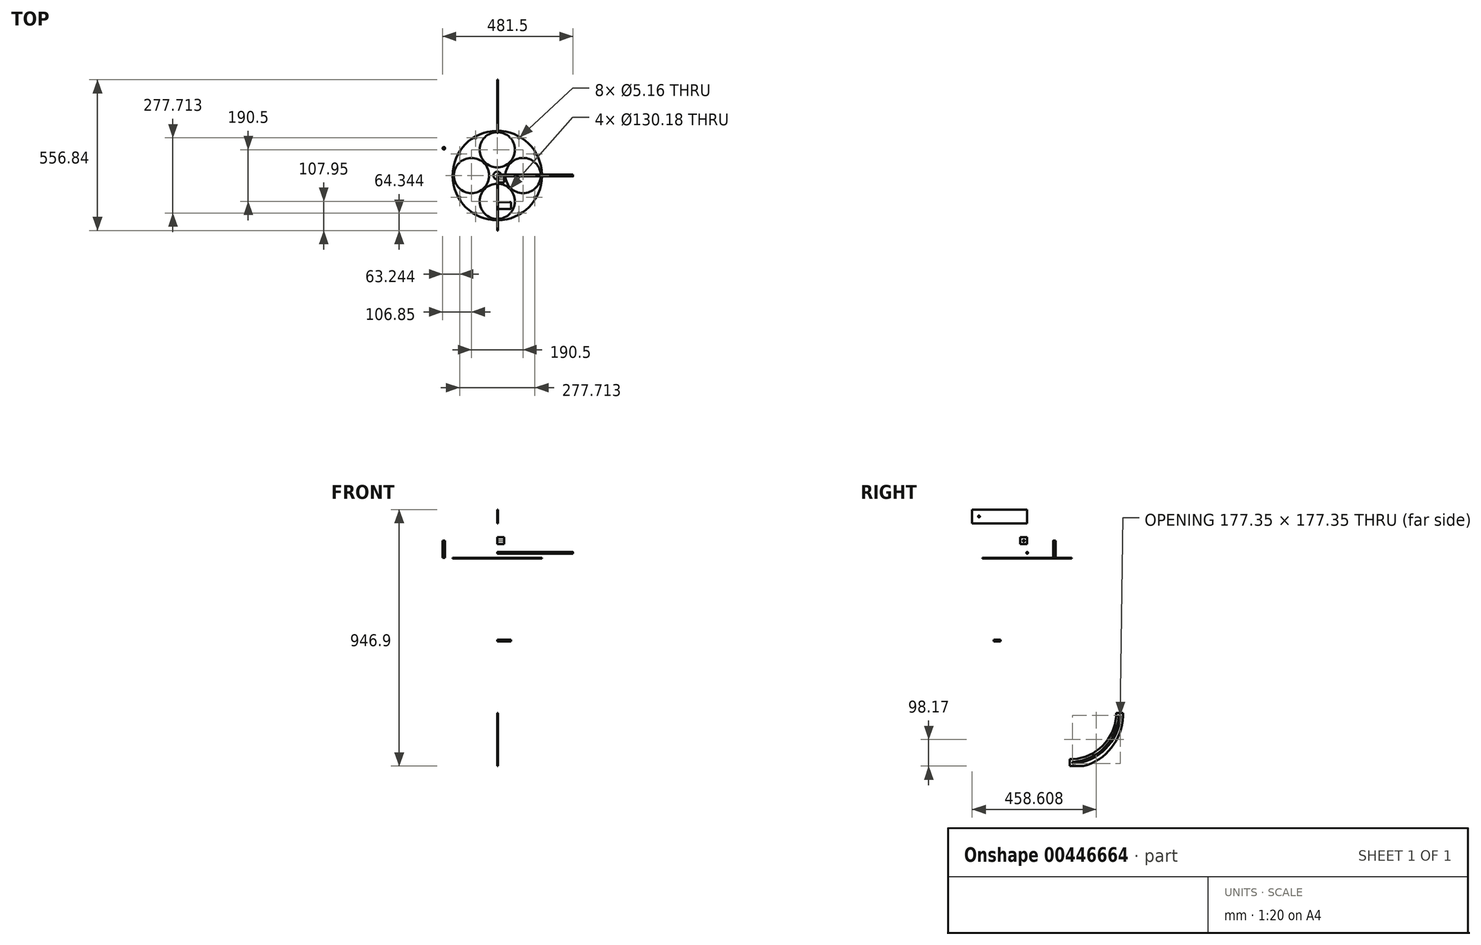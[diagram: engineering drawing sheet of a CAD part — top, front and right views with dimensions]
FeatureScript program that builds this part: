
annotation { "Feature Type Name" : "Feature", "Feature Type Description" : "" }
export const myFeature = defineFeature(function(context is Context, id is Id, definition is map)
    precondition{}
    {
        {
            var Q0;
            Q0=qCreatedBy(makeId("Top.planeOp"),FACE);
            var sketch = newSketch(context, id + "F0", { "sketchPlane" : qUnion([Q0])});
            skCircle(sketch, "E0", {"center": v(0, 0) * mm, "radius": 165.1 * mm});
            skCircle(sketch, "E1", {"center": v(0, 95.25) * mm, "radius": 65.09 * mm});
            skCircle(sketch, "E2", {"center": v(95.25, 0) * mm, "radius": 65.09 * mm});
            skCircle(sketch, "E3", {"center": v(0, -95.25) * mm, "radius": 65.09 * mm});
            skCircle(sketch, "E4", {"center": v(-95.25, 0) * mm, "radius": 65.09 * mm});
            skCircle(sketch, "E5", {"center": v(138.86, 80.17) * mm, "radius": 2.58 * mm});
            skCircle(sketch, "E6.1.0", {"center": v(80.17, 138.86) * mm, "radius": 2.58 * mm});
            skCircle(sketch, "E7.1.3.0", {"center": v(-80.17, 138.86) * mm, "radius": 2.58 * mm});
            skCircle(sketch, "E7.1.4.0", {"center": v(-138.86, 80.17) * mm, "radius": 2.58 * mm});
            skCircle(sketch, "E7.1.6.0", {"center": v(-138.86, -80.17) * mm, "radius": 2.58 * mm});
            skCircle(sketch, "E7.1.7.0", {"center": v(-80.17, -138.86) * mm, "radius": 2.58 * mm});
            skCircle(sketch, "E8.1.9.0", {"center": v(80.17, -138.86) * mm, "radius": 2.58 * mm});
            skCircle(sketch, "E8.1.10.0", {"center": v(138.86, -80.17) * mm, "radius": 2.58 * mm});
            skCircle(sketch, "E9", {"center": v(0, 0) * mm, "radius": 14.22 * mm});
            skSolve(sketch);
        }
        {
            var Q0;
            Q0=makeQuery(id+"F0.imprint","IMPRINT",FACE,{"disambiguationData":[TD([[makeQuery(id+"F0.imprint","IMPRINT",EDGE,{"derivedFrom":sQuery(id+"F0.wireOp",EDGE,"E0")}),1.0]])]});
            extrude(context, id + "F1", {"entities" : qUnion([Q0]), "depth" : 2.54 * mm});
        }
        {
            var Q0;
            Q0=makeQuery(id+"F1.opExtrude","CAP_FACE",FACE,{"disambiguationData":[OSD([sQuery(id+"F0.wireOp",EDGE,"E0"),sQuery(id+"F0.wireOp",EDGE,"E1"),sQuery(id+"F0.wireOp",EDGE,"E2"),sQuery(id+"F0.wireOp",EDGE,"E3"),sQuery(id+"F0.wireOp",EDGE,"E4"),sQuery(id+"F0.wireOp",EDGE,"E5"),sQuery(id+"F0.wireOp",EDGE,"E6.1.0"),sQuery(id+"F0.wireOp",EDGE,"E7.1.3.0"),sQuery(id+"F0.wireOp",EDGE,"E7.1.4.0"),sQuery(id+"F0.wireOp",EDGE,"E7.1.6.0"),sQuery(id+"F0.wireOp",EDGE,"E7.1.7.0"),sQuery(id+"F0.wireOp",EDGE,"E8.1.9.0"),sQuery(id+"F0.wireOp",EDGE,"E8.1.10.0")])],"isStart":false});
            var sketch = newSketch(context, id + "F2", { "sketchPlane" : qUnion([Q0])});
            skCircle(sketch, "E10", {"center": v(-197.34, 100.57) * mm, "radius": 4.76 * mm});
            skSolve(sketch);
        }
        {
            var Q0;
            Q0=makeQuery(id+"F2.imprint","IMPRINT",FACE,{"disambiguationData":[TD([[makeQuery(id+"F2.imprint","IMPRINT",EDGE,{"derivedFrom":sQuery(id+"F2.wireOp",EDGE,"E10")}),1.0]])]});
            extrude(context, id + "F3", {"entities" : qUnion([Q0]), "depth" : 63.5 * mm});
        }
        {
            var Q0;
            Q0=qCreatedBy(makeId("Right.planeOp"),FACE);
            var sketch = newSketch(context, id + "F4", { "sketchPlane" : qUnion([Q0])});
            skLineSegment(sketch, "E11.bottom", {"start": v(0, 130.26) * mm, "end": v(-203.2, 130.26) * mm});
            skLineSegment(sketch, "E11.top", {"start": v(0, 181.06) * mm, "end": v(-203.2, 181.06) * mm});
            skLineSegment(sketch, "E11.left", {"start": v(0, 130.26) * mm, "end": v(0, 181.06) * mm});
            skLineSegment(sketch, "E11.right", {"start": v(-203.2, 130.26) * mm, "end": v(-203.2, 181.06) * mm});
            skLineSegment(sketch, "E12.0", {"start": v(-152.4, 132.42) * mm, "end": v(-152.4, 183.22) * mm, "construction": true});
            skLineSegment(sketch, "E13.0", {"start": v(-177.8, 132.42) * mm, "end": v(-177.8, 183.22) * mm, "construction": true});
            skLineSegment(sketch, "E14.0", {"start": v(0, 155.66) * mm, "end": v(-203.2, 155.66) * mm, "construction": true});
            skCircle(sketch, "E15", {"center": v(-177.8, 155.66) * mm, "radius": 3.18 * mm});
            skLineSegment(sketch, "E16.0", {"start": v(-82.55, 130.26) * mm, "end": v(-82.55, 181.06) * mm, "construction": true});
            skLineSegment(sketch, "E17.0", {"start": v(38.1, 130.26) * mm, "end": v(38.1, 181.06) * mm, "construction": true});
            skLineSegment(sketch, "E18.0", {"start": v(-266.7, 132.42) * mm, "end": v(-266.7, 183.22) * mm, "construction": true});
            skSolve(sketch);
        }
        {
            var Q0;
            Q0 = qSketchRegion(id + "F4", true);
            extrude(context, id + "F5", {"entities" : qUnion([Q0]), "depth" : 2.54 * mm});
        }
        {
            var Q0;
            Q0=qCreatedBy(makeId("Right.planeOp"),FACE);
            var sketch = newSketch(context, id + "F6", { "sketchPlane" : qUnion([Q0])});
            skCircle(sketch, "E19", {"center": v(0, 21.4) * mm, "radius": 3.18 * mm});
            skSolve(sketch);
        }
        {
            var Q0;
            Q0 = qSketchRegion(id + "F6", true);
            extrude(context, id + "F7", {"entities" : qUnion([Q0]), "depth" : 279.4 * mm});
        }
        {
            var Q0;
            Q0=qCreatedBy(makeId("Right.planeOp"),FACE);
            var sketch = newSketch(context, id + "F8", { "sketchPlane" : qUnion([Q0])});
            skLineSegment(sketch, "E20.bottom", {"start": v(0, 53.35) * mm, "end": v(-25.4, 53.35) * mm});
            skLineSegment(sketch, "E20.top", {"start": v(0, 78.75) * mm, "end": v(-25.4, 78.75) * mm});
            skLineSegment(sketch, "E20.left", {"start": v(0, 53.35) * mm, "end": v(0, 78.75) * mm});
            skLineSegment(sketch, "E20.right", {"start": v(-25.4, 53.35) * mm, "end": v(-25.4, 78.75) * mm});
            skLineSegment(sketch, "E21.0", {"start": v(-12.7, 53.35) * mm, "end": v(-12.7, 78.75) * mm, "construction": true});
            skLineSegment(sketch, "E22.0", {"start": v(0, 66.05) * mm, "end": v(-25.4, 66.05) * mm, "construction": true});
            skCircle(sketch, "E23", {"center": v(-12.7, 66.05) * mm, "radius": 3.18 * mm});
            skSolve(sketch);
        }
        {
            var Q0;
            Q0=makeQuery(id+"F8.imprint","IMPRINT",FACE,{"disambiguationData":[TD([[makeQuery(id+"F8.imprint","IMPRINT",EDGE,{"derivedFrom":sQuery(id+"F8.wireOp",EDGE,"E20.bottom")}),-1.0]])]});
            extrude(context, id + "F9", {"entities" : qUnion([Q0]), "depth" : 25.4 * mm});
        }
        {
            var Q0;
            Q0=qCreatedBy(makeId("Right.planeOp"),FACE);
            var sketch = newSketch(context, id + "F10", { "sketchPlane" : qUnion([Q0])});
            skLineSegment(sketch, "E24", {"start": v(328.24, -569.46) * mm, "end": v(353.64, -569.46) * mm});
            skLineSegment(sketch, "E25", {"start": v(157.2, -740.44) * mm, "end": v(157.2, -765.84) * mm});
            skArc(sketch, "E26", {"start": v(169.9, -772.24) * mm, "mid": v(169.9, -772.23) * mm, "end": v(169.9, -772.23) * mm});
            skArc(sketch, "E27", {"start": v(169.9, -740.44) * mm, "mid": v(278.47, -690.72) * mm, "end": v(328.24, -582.16) * mm});
            skLineSegment(sketch, "E28.0", {"start": v(328.24, -582.16) * mm, "end": v(353.64, -582.16) * mm, "construction": true});
            skLineSegment(sketch, "E29.0", {"start": v(169.9, -740.44) * mm, "end": v(169.9, -772.23) * mm, "construction": true});
            skArc(sketch, "E30", {"start": v(344.08, -582.38) * mm, "mid": v(341.02, -579) * mm, "end": v(337.74, -582.16) * mm});
            skArc(sketch, "E31", {"start": v(169.9, -750) * mm, "mid": v(166.73, -753.29) * mm, "end": v(170.12, -756.34) * mm});
            skArc(sketch, "E32", {"start": v(169.9, -756.36) * mm, "mid": v(289.66, -701.92) * mm, "end": v(344.1, -582.16) * mm});
            skArc(sketch, "E33", {"start": v(169.68, -750) * mm, "mid": v(285.17, -697.43) * mm, "end": v(337.75, -581.95) * mm});
            skArc(sketch, "E34", {"start": v(142.3, -759.39) * mm, "mid": v(286.92, -706.21) * mm, "end": v(340.5, -561.75) * mm, "construction": true});
            skLineSegment(sketch, "E35", {"start": v(353.64, -582.16) * mm, "end": v(353.64, -569.46) * mm});
            skLineSegment(sketch, "E36", {"start": v(328.24, -582.16) * mm, "end": v(328.24, -569.46) * mm});
            skPoint(sketch, "E37.orphan", {"position": v(353.64, -567.09) * mm});
            skLineSegment(sketch, "E38", {"start": v(169.9, -740.44) * mm, "end": v(157.2, -740.44) * mm});
            skLineSegment(sketch, "E39.0", {"start": v(208.26, -765.84) * mm, "end": v(157.2, -765.84) * mm});
            skArc(sketch, "E40.trimOffspring", {"start": v(208.26, -765.84) * mm, "mid": v(311.25, -697.98) * mm, "end": v(353.64, -582.16) * mm});
            skSolve(sketch);
        }
        {
            var Q0;
            Q0 = qSketchRegion(id + "F10", true);
            extrude(context, id + "F11", {"entities" : qUnion([Q0]), "depth" : 2.54 * mm});
        }
        {
            var Q0;
            Q0=qCreatedBy(makeId("Right.planeOp"),FACE);
            var sketch = newSketch(context, id + "F12", { "sketchPlane" : qUnion([Q0])});
            skLineSegment(sketch, "E41.bottom", {"start": v(-123.46, -305.47) * mm, "end": v(-98.06, -305.47) * mm});
            skLineSegment(sketch, "E41.top", {"start": v(-123.46, -299.12) * mm, "end": v(-98.06, -299.12) * mm});
            skLineSegment(sketch, "E41.left", {"start": v(-123.46, -305.47) * mm, "end": v(-123.46, -299.12) * mm});
            skLineSegment(sketch, "E41.right", {"start": v(-98.06, -305.47) * mm, "end": v(-98.06, -299.12) * mm});
            skSolve(sketch);
        }
        {
            var Q0;
            Q0 = qSketchRegion(id + "F12", true);
            extrude(context, id + "F13", {"entities" : qUnion([Q0]), "depth" : 50.8 * mm});
        }
    });
